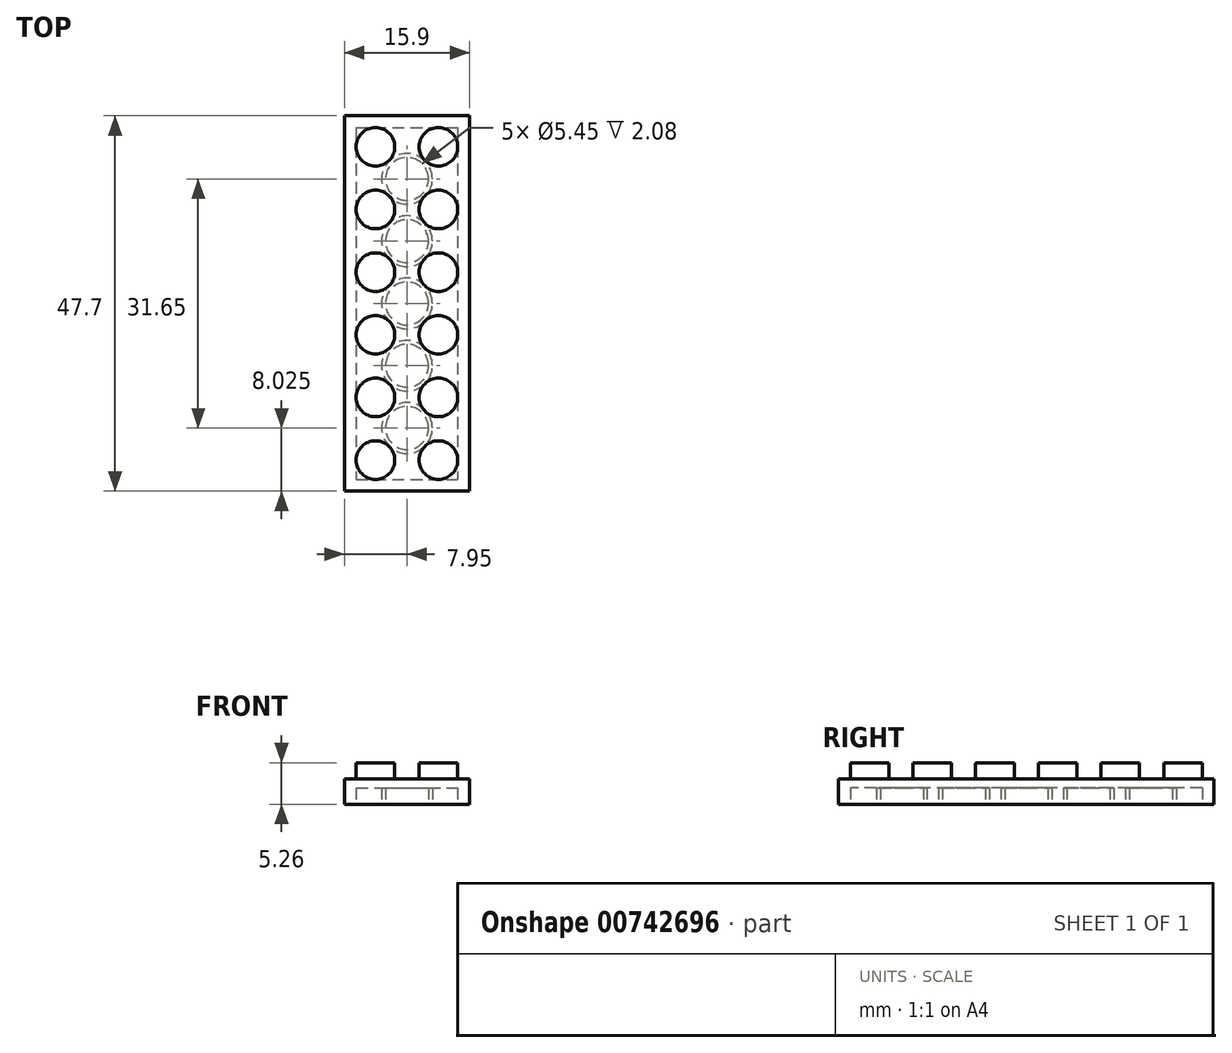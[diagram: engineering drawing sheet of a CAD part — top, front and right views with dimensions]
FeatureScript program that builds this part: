
annotation { "Feature Type Name" : "Feature", "Feature Type Description" : "" }
export const myFeature = defineFeature(function(context is Context, id is Id, definition is map)
    precondition{}
    {
        {
            var Q0;
            Q0=qCreatedBy(makeId("Top.planeOp"),FACE);
            var sketch = newSketch(context, id + "F0", { "sketchPlane" : qUnion([Q0])});
            skLineSegment(sketch, "E0.bottom", {"start": v(0, 0) * mm, "end": v(15.9, 0) * mm});
            skLineSegment(sketch, "E0.top", {"start": v(0, -47.7) * mm, "end": v(15.9, -47.7) * mm});
            skLineSegment(sketch, "E0.left", {"start": v(0, 0) * mm, "end": v(0, -47.7) * mm});
            skLineSegment(sketch, "E0.right", {"start": v(15.9, 0) * mm, "end": v(15.9, -47.7) * mm});
            skCircle(sketch, "E1", {"center": v(3.95, -3.95) * mm, "radius": 2.45 * mm});
            skCircle(sketch, "E2", {"center": v(11.95, -3.95) * mm, "radius": 2.45 * mm});
            skCircle(sketch, "E3", {"center": v(3.95, -11.9) * mm, "radius": 2.45 * mm});
            skCircle(sketch, "E4", {"center": v(3.95, -19.87) * mm, "radius": 2.45 * mm});
            skCircle(sketch, "E5", {"center": v(3.95, -27.83) * mm, "radius": 2.45 * mm});
            skCircle(sketch, "E6", {"center": v(3.95, -35.8) * mm, "radius": 2.45 * mm});
            skCircle(sketch, "E7", {"center": v(3.95, -43.75) * mm, "radius": 2.45 * mm});
            skCircle(sketch, "E8", {"center": v(11.95, -11.9) * mm, "radius": 2.45 * mm});
            skCircle(sketch, "E9", {"center": v(11.95, -19.87) * mm, "radius": 2.45 * mm});
            skCircle(sketch, "E10", {"center": v(11.95, -27.83) * mm, "radius": 2.45 * mm});
            skCircle(sketch, "E11", {"center": v(11.95, -35.8) * mm, "radius": 2.45 * mm});
            skCircle(sketch, "E12", {"center": v(11.95, -43.75) * mm, "radius": 2.45 * mm});
            skSolve(sketch);
        }
        {
            var Q0;
            Q0=makeQuery(id+"F0.imprint","IMPRINT",FACE,{"disambiguationData":[TD([[makeQuery(id+"F0.imprint","IMPRINT",EDGE,{"derivedFrom":sQuery(id+"F0.wireOp",EDGE,"E0.bottom")}),-1.0]])]});
            extrude(context, id + "F1", {"entities" : qUnion([Q0]), "depth" : 3.18 * mm, "offsetDistance" : 25 * mm});
        }
        {
            var Q0;
            Q0=makeQuery(id+"F0.imprint","IMPRINT",FACE,{"disambiguationData":[TD([[makeQuery(id+"F0.imprint","IMPRINT",EDGE,{"derivedFrom":sQuery(id+"F0.wireOp",EDGE,"E1")}),1.0]])]});
            var Q1;
            Q1=makeQuery(id+"F0.imprint","IMPRINT",FACE,{"disambiguationData":[TD([[makeQuery(id+"F0.imprint","IMPRINT",EDGE,{"derivedFrom":sQuery(id+"F0.wireOp",EDGE,"E2")}),1.0]])]});
            var Q2;
            Q2=makeQuery(id+"F0.imprint","IMPRINT",FACE,{"disambiguationData":[TD([[makeQuery(id+"F0.imprint","IMPRINT",EDGE,{"derivedFrom":sQuery(id+"F0.wireOp",EDGE,"E8")}),1.0]])]});
            var Q3;
            Q3=makeQuery(id+"F0.imprint","IMPRINT",FACE,{"disambiguationData":[TD([[makeQuery(id+"F0.imprint","IMPRINT",EDGE,{"derivedFrom":sQuery(id+"F0.wireOp",EDGE,"E3")}),1.0]])]});
            var Q4;
            Q4=makeQuery(id+"F0.imprint","IMPRINT",FACE,{"disambiguationData":[TD([[makeQuery(id+"F0.imprint","IMPRINT",EDGE,{"derivedFrom":sQuery(id+"F0.wireOp",EDGE,"E4")}),1.0]])]});
            var Q5;
            Q5=makeQuery(id+"F0.imprint","IMPRINT",FACE,{"disambiguationData":[TD([[makeQuery(id+"F0.imprint","IMPRINT",EDGE,{"derivedFrom":sQuery(id+"F0.wireOp",EDGE,"E9")}),1.0]])]});
            var Q6;
            Q6=makeQuery(id+"F0.imprint","IMPRINT",FACE,{"disambiguationData":[TD([[makeQuery(id+"F0.imprint","IMPRINT",EDGE,{"derivedFrom":sQuery(id+"F0.wireOp",EDGE,"E10")}),1.0]])]});
            var Q7;
            Q7=makeQuery(id+"F0.imprint","IMPRINT",FACE,{"disambiguationData":[TD([[makeQuery(id+"F0.imprint","IMPRINT",EDGE,{"derivedFrom":sQuery(id+"F0.wireOp",EDGE,"E5")}),1.0]])]});
            var Q8;
            Q8=makeQuery(id+"F0.imprint","IMPRINT",FACE,{"disambiguationData":[TD([[makeQuery(id+"F0.imprint","IMPRINT",EDGE,{"derivedFrom":sQuery(id+"F0.wireOp",EDGE,"E6")}),1.0]])]});
            var Q9;
            Q9=makeQuery(id+"F0.imprint","IMPRINT",FACE,{"disambiguationData":[TD([[makeQuery(id+"F0.imprint","IMPRINT",EDGE,{"derivedFrom":sQuery(id+"F0.wireOp",EDGE,"E11")}),1.0]])]});
            var Q10;
            Q10=makeQuery(id+"F0.imprint","IMPRINT",FACE,{"disambiguationData":[TD([[makeQuery(id+"F0.imprint","IMPRINT",EDGE,{"derivedFrom":sQuery(id+"F0.wireOp",EDGE,"E12")}),1.0]])]});
            var Q11;
            Q11=makeQuery(id+"F0.imprint","IMPRINT",FACE,{"disambiguationData":[TD([[makeQuery(id+"F0.imprint","IMPRINT",EDGE,{"derivedFrom":sQuery(id+"F0.wireOp",EDGE,"E7")}),1.0]])]});
            extrude(context, id + "F2", {"entities" : qUnion([Q0, Q1, Q2, Q3, Q4, Q5, Q6, Q7, Q8, Q9, Q10, Q11]), "operationType" : NewBodyOperationType.ADD, "depth" : 5.26 * mm, "offsetDistance" : 25 * mm});
        }
        {
            var Q0;
            {var subQ0=sQuery(id+"F0.wireOp",EDGE,"E12");var subQ1=sQuery(id+"F0.wireOp",EDGE,"E11");var subQ2=sQuery(id+"F0.wireOp",EDGE,"E10");var subQ3=sQuery(id+"F0.wireOp",EDGE,"E9");var subQ4=sQuery(id+"F0.wireOp",EDGE,"E8");var subQ5=sQuery(id+"F0.wireOp",EDGE,"E7");var subQ6=sQuery(id+"F0.wireOp",EDGE,"E6");var subQ7=sQuery(id+"F0.wireOp",EDGE,"E5");var subQ8=sQuery(id+"F0.wireOp",EDGE,"E4");var subQ9=sQuery(id+"F0.wireOp",EDGE,"E3");var subQ10=sQuery(id+"F0.wireOp",EDGE,"E2");var subQ11=sQuery(id+"F0.wireOp",EDGE,"E1");Q0=makeQuery(id+"F2.boolean.opBoolean","MERGE",FACE,{"derivedFrom":[makeQuery(id+"F1.opExtrude","CAP_FACE",FACE,{"disambiguationData":[OSD([sQuery(id+"F0.wireOp",EDGE,"E0.bottom"),sQuery(id+"F0.wireOp",EDGE,"E0.top"),sQuery(id+"F0.wireOp",EDGE,"E0.left"),sQuery(id+"F0.wireOp",EDGE,"E0.right"),subQ11,subQ10,subQ9,subQ8,subQ7,subQ6,subQ5,subQ4,subQ3,subQ2,subQ1,subQ0])],"isStart":true}),makeQuery(id+"F2.opExtrude","CAP_FACE",FACE,{"disambiguationData":[OSD([subQ11])],"isStart":true}),makeQuery(id+"F2.opExtrude","CAP_FACE",FACE,{"disambiguationData":[OSD([subQ10])],"isStart":true}),makeQuery(id+"F2.opExtrude","CAP_FACE",FACE,{"disambiguationData":[OSD([subQ9])],"isStart":true}),makeQuery(id+"F2.opExtrude","CAP_FACE",FACE,{"disambiguationData":[OSD([subQ8])],"isStart":true}),makeQuery(id+"F2.opExtrude","CAP_FACE",FACE,{"disambiguationData":[OSD([subQ7])],"isStart":true}),makeQuery(id+"F2.opExtrude","CAP_FACE",FACE,{"disambiguationData":[OSD([subQ6])],"isStart":true}),makeQuery(id+"F2.opExtrude","CAP_FACE",FACE,{"disambiguationData":[OSD([subQ5])],"isStart":true}),makeQuery(id+"F2.opExtrude","CAP_FACE",FACE,{"disambiguationData":[OSD([subQ4])],"isStart":true}),makeQuery(id+"F2.opExtrude","CAP_FACE",FACE,{"disambiguationData":[OSD([subQ3])],"isStart":true}),makeQuery(id+"F2.opExtrude","CAP_FACE",FACE,{"disambiguationData":[OSD([subQ2])],"isStart":true}),makeQuery(id+"F2.opExtrude","CAP_FACE",FACE,{"disambiguationData":[OSD([subQ1])],"isStart":true}),makeQuery(id+"F2.opExtrude","CAP_FACE",FACE,{"disambiguationData":[OSD([subQ0])],"isStart":true})]});}
            var sketch = newSketch(context, id + "F3", { "sketchPlane" : qUnion([Q0])});
            skLineSegment(sketch, "E13.0", {"start": v(1.5, 1.5) * mm, "end": v(1.5, 46.2) * mm});
            skLineSegment(sketch, "E13.1", {"start": v(1.5, 1.5) * mm, "end": v(14.4, 1.5) * mm});
            skLineSegment(sketch, "E13.2", {"start": v(14.4, 1.5) * mm, "end": v(14.4, 46.2) * mm});
            skLineSegment(sketch, "E13.3", {"start": v(1.5, 46.2) * mm, "end": v(14.4, 46.2) * mm});
            skCircle(sketch, "E14", {"center": v(7.95, 39.68) * mm, "radius": 3.23 * mm});
            skPoint(sketch, "E14.centerSnap0", {"position": v(7.95, 47.7) * mm});
            skCircle(sketch, "E15", {"center": v(7.95, 31.76) * mm, "radius": 3.23 * mm});
            skCircle(sketch, "E16", {"center": v(7.95, 23.85) * mm, "radius": 3.23 * mm});
            skPoint(sketch, "E16.centerSnap0", {"position": v(1.5, 23.85) * mm});
            skCircle(sketch, "E17", {"center": v(7.95, 15.94) * mm, "radius": 3.23 * mm});
            skCircle(sketch, "E18", {"center": v(7.95, 8.03) * mm, "radius": 3.23 * mm});
            skCircle(sketch, "E19", {"center": v(7.95, 39.68) * mm, "radius": 2.73 * mm});
            skCircle(sketch, "E20", {"center": v(7.95, 31.76) * mm, "radius": 2.73 * mm});
            skCircle(sketch, "E21", {"center": v(7.95, 23.85) * mm, "radius": 2.73 * mm});
            skCircle(sketch, "E22", {"center": v(7.95, 15.94) * mm, "radius": 2.73 * mm});
            skCircle(sketch, "E23", {"center": v(7.95, 8.03) * mm, "radius": 2.73 * mm});
            skSolve(sketch);
        }
        {
            var Q0;
            Q0=makeQuery(id+"F3.imprint","IMPRINT",FACE,{"disambiguationData":[TD([[makeQuery(id+"F3.imprint","IMPRINT",EDGE,{"derivedFrom":sQuery(id+"F3.wireOp",EDGE,"E13.0")}),-1.0]])]});
            var Q1;
            Q1=makeQuery(id+"F3.imprint","IMPRINT",FACE,{"disambiguationData":[TD([[makeQuery(id+"F3.imprint","IMPRINT",EDGE,{"derivedFrom":sQuery(id+"F3.wireOp",EDGE,"E19")}),1.0]])]});
            var Q2;
            Q2=makeQuery(id+"F3.imprint","IMPRINT",FACE,{"disambiguationData":[TD([[makeQuery(id+"F3.imprint","IMPRINT",EDGE,{"derivedFrom":sQuery(id+"F3.wireOp",EDGE,"E20")}),1.0]])]});
            var Q3;
            Q3=makeQuery(id+"F3.imprint","IMPRINT",FACE,{"disambiguationData":[TD([[makeQuery(id+"F3.imprint","IMPRINT",EDGE,{"derivedFrom":sQuery(id+"F3.wireOp",EDGE,"E21")}),1.0]])]});
            var Q4;
            Q4=makeQuery(id+"F3.imprint","IMPRINT",FACE,{"disambiguationData":[TD([[makeQuery(id+"F3.imprint","IMPRINT",EDGE,{"derivedFrom":sQuery(id+"F3.wireOp",EDGE,"E22")}),1.0]])]});
            var Q5;
            Q5=makeQuery(id+"F3.imprint","IMPRINT",FACE,{"disambiguationData":[TD([[makeQuery(id+"F3.imprint","IMPRINT",EDGE,{"derivedFrom":sQuery(id+"F3.wireOp",EDGE,"E23")}),1.0]])]});
            extrude(context, id + "F4", {"entities" : qUnion([Q0, Q1, Q2, Q3, Q4, Q5]), "operationType" : NewBodyOperationType.REMOVE, "oppositeDirection" : true, "depth" : 2.08 * mm, "offsetDistance" : 25 * mm});
        }
    });
